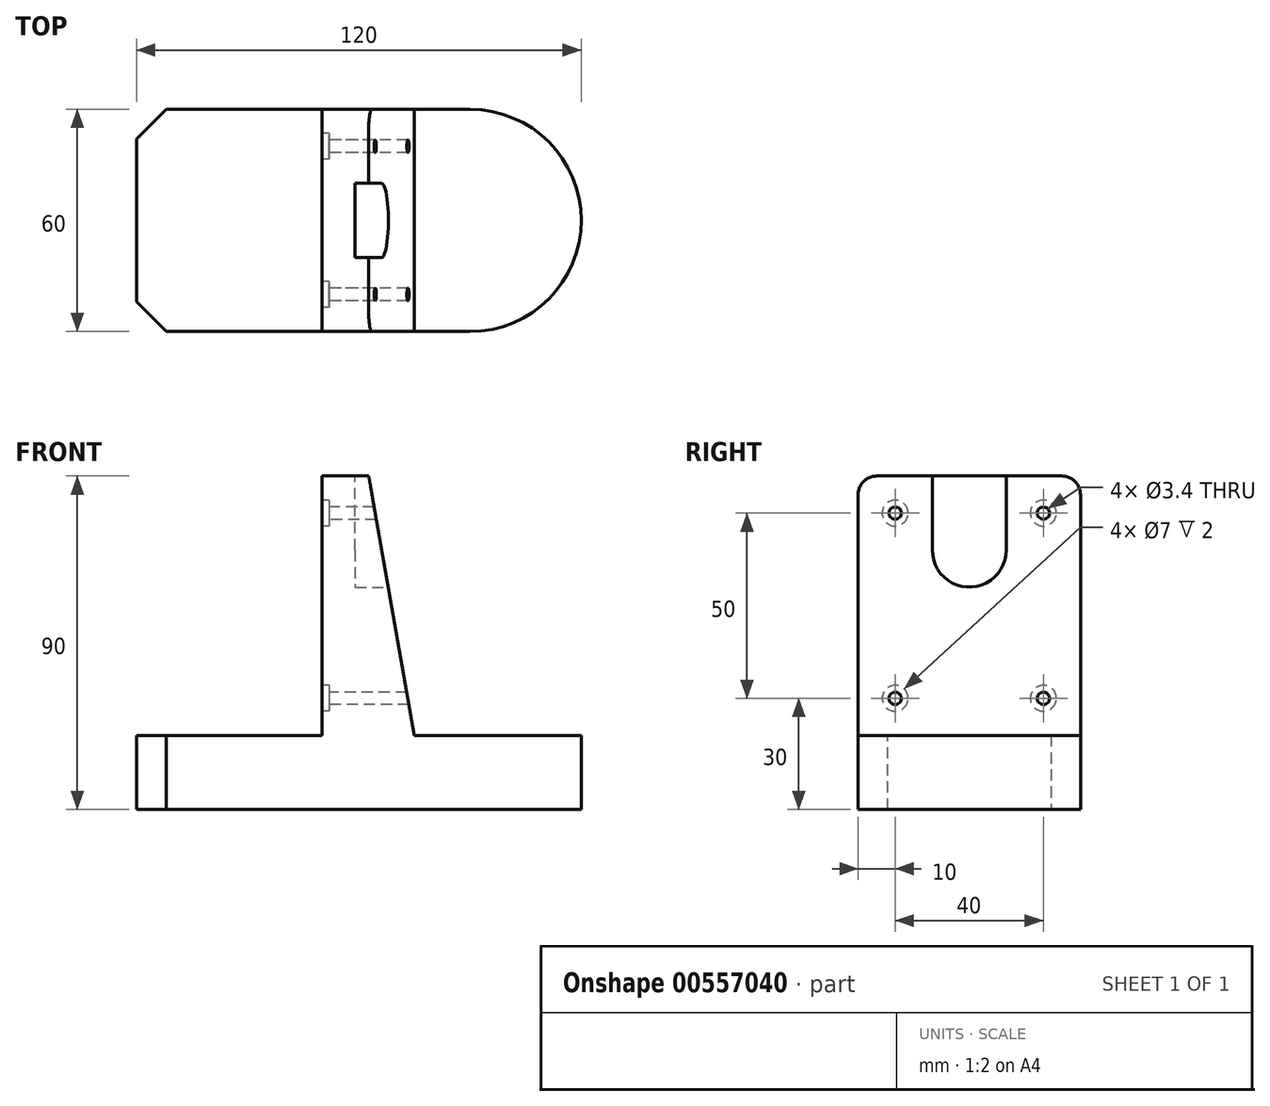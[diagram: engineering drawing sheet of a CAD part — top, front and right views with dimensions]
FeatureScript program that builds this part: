
annotation { "Feature Type Name" : "Feature", "Feature Type Description" : "" }
export const myFeature = defineFeature(function(context is Context, id is Id, definition is map)
    precondition{}
    {
        {
            var Q0;
            Q0=qCreatedBy(makeId("Front.planeOp"),FACE);
            var sketch = newSketch(context, id + "F0", { "sketchPlane" : qUnion([Q0])});
            skLineSegment(sketch, "E0", {"start": v(0, 0) * mm, "end": v(120, 0) * mm});
            skLineSegment(sketch, "E1", {"start": v(0, 0) * mm, "end": v(0, 20) * mm});
            skLineSegment(sketch, "E2", {"start": v(0, 20) * mm, "end": v(50, 20) * mm});
            skLineSegment(sketch, "E3", {"start": v(120, 0) * mm, "end": v(120, 20) * mm});
            skLineSegment(sketch, "E4", {"start": v(75, 20) * mm, "end": v(120, 20) * mm});
            skLineSegment(sketch, "E5", {"start": v(75, 20) * mm, "end": v(75, 90) * mm});
            skLineSegment(sketch, "E6", {"start": v(50, 20) * mm, "end": v(50, 90) * mm});
            skLineSegment(sketch, "E7", {"start": v(50, 90) * mm, "end": v(75, 90) * mm});
            skSolve(sketch);
        }
        {
            var Q0;
            Q0=qSketchRegion(id+"F0",true);
            extrude(context, id + "F1", {"entities" : qUnion([Q0]), "endBound" : BoundingType.SYMMETRIC, "depth" : 60 * mm, "offsetDistance" : 25 * mm});
        }
        {
            var Q0;
            Q0=makeQuery(id+"F1.opExtrude","CAP_EDGE",EDGE,{"disambiguationData":[OSD([sQuery(id+"F0.wireOp",EDGE,"E3")])],"isStart":false});
            var Q1;
            Q1=makeQuery(id+"F1.opExtrude","CAP_EDGE",EDGE,{"disambiguationData":[OSD([sQuery(id+"F0.wireOp",EDGE,"E3")])],"isStart":true});
            fillet(context, id + "F2", {"entities" : qUnion([Q0, Q1]), "radius" : 30 * mm, "tangentPropagation" : true, "allowEdgeOverflow" : false});
        }
        {
            var Q0;
            Q0=makeQuery(id+"F1.opExtrude","SWEPT_FACE",FACE,{"disambiguationData":[OSD([sQuery(id+"F0.wireOp",EDGE,"E6")])]});
            var sketch = newSketch(context, id + "F3", { "sketchPlane" : qUnion([Q0])});
            skLineSegment(sketch, "E8", {"start": v(-20, 30) * mm, "end": v(20, 30) * mm, "construction": true});
            skLineSegment(sketch, "E9", {"start": v(0, 0) * mm, "end": v(0, 92.48) * mm, "construction": true});
            skPoint(sketch, "E9.endSnap0", {"position": v(0, 90) * mm});
            skLineSegment(sketch, "E10", {"start": v(-20, 30) * mm, "end": v(-20, 80) * mm, "construction": true});
            skLineSegment(sketch, "E11", {"start": v(-20, 80) * mm, "end": v(20, 80) * mm, "construction": true});
            skLineSegment(sketch, "E12", {"start": v(20, 80) * mm, "end": v(20, 30) * mm, "construction": true});
            skCircle(sketch, "E13", {"center": v(-20, 80) * mm, "radius": 3.5 * mm});
            skSolve(sketch);
        }
        {
            var Q0;
            Q0=sQuery(id+"F3.wireOp",VERTEX,"E13.center");
            var Q1;
            Q1=sQuery(id+"F3.wireOp",VERTEX,"E8.start");
            var Q2;
            Q2=sQuery(id+"F3.wireOp",VERTEX,"E12.end");
            var Q3;
            Q3=sQuery(id+"F3.wireOp",VERTEX,"E12.start");
            var Q4;
            Q4=makeQuery(id+"F1.opExtrude","SWEPT_BODY",BODY,{"disambiguationData":[OSD([sQuery(id+"F0.wireOp",EDGE,"E0"),sQuery(id+"F0.wireOp",EDGE,"E1"),sQuery(id+"F0.wireOp",EDGE,"E2"),sQuery(id+"F0.wireOp",EDGE,"E3"),sQuery(id+"F0.wireOp",EDGE,"E4"),sQuery(id+"F0.wireOp",EDGE,"E5"),sQuery(id+"F0.wireOp",EDGE,"E6"),sQuery(id+"F0.wireOp",EDGE,"E7")])]});
            hole(context, id + "F4", {"style" : HoleStyle.C_BORE, "endStyle" : HoleEndStyle.THROUGH, "holeDiameter" : 3.4 * mm, "cBoreDiameter" : 7 * mm, "cBoreDepth" : 2 * mm, "isTappedThrough" : true, "tappedDepth" : 12 * mm, "tapClearance" : 3, "locations" : qUnion([Q0, Q1, Q2, Q3]), "scope" : qUnion([Q4])});
        }
        {
            var Q0;
            Q0=makeQuery(id+"F1.opExtrude","CAP_EDGE",EDGE,{"disambiguationData":[OSD([sQuery(id+"F0.wireOp",EDGE,"E1")])],"isStart":true});
            var Q1;
            Q1=makeQuery(id+"F1.opExtrude","CAP_EDGE",EDGE,{"disambiguationData":[OSD([sQuery(id+"F0.wireOp",EDGE,"E1")])],"isStart":false});
            chamfer(context, id + "F5", {"entities" : qUnion([Q0, Q1]), "width" : 8 * mm, "tangentPropagation" : true});
        }
        {
            var Q0;
            Q0=makeQuery(id+"F1.opExtrude","CAP_FACE",FACE,{"disambiguationData":[OSD([sQuery(id+"F0.wireOp",EDGE,"E0"),sQuery(id+"F0.wireOp",EDGE,"E1"),sQuery(id+"F0.wireOp",EDGE,"E2"),sQuery(id+"F0.wireOp",EDGE,"E3"),sQuery(id+"F0.wireOp",EDGE,"E4"),sQuery(id+"F0.wireOp",EDGE,"E5"),sQuery(id+"F0.wireOp",EDGE,"E6"),sQuery(id+"F0.wireOp",EDGE,"E7")])],"isStart":false});
            var sketch = newSketch(context, id + "F6", { "sketchPlane" : qUnion([Q0])});
            skLineSegment(sketch, "E14", {"start": v(75, 20) * mm, "end": v(62.66, 90) * mm});
            skSolve(sketch);
        }
        {
            var Q0;
            Q0=makeQuery(id+"F1.opExtrude","SWEPT_FACE",FACE,{"disambiguationData":[OSD([sQuery(id+"F0.wireOp",EDGE,"E5")])]});
            var sketch = newSketch(context, id + "F7", { "sketchPlane" : qUnion([Q0])});
            skLineSegment(sketch, "E15", {"start": v(0, -24) * mm, "end": v(0, 77.1) * mm, "construction": true});
            skLineSegment(sketch, "E16", {"start": v(-10, 70) * mm, "end": v(10, 70) * mm, "construction": true});
            skCircle(sketch, "E17", {"center": v(0, 70) * mm, "radius": 10 * mm});
            skLineSegment(sketch, "E18", {"start": v(-10, 70) * mm, "end": v(-10, 90) * mm});
            skLineSegment(sketch, "E19", {"start": v(10, 70) * mm, "end": v(10, 90) * mm});
            skSolve(sketch);
        }
        {
            var Q0;
            Q0=makeQuery(id+"F1.opExtrude","CAP_FACE",FACE,{"disambiguationData":[OSD([sQuery(id+"F0.wireOp",EDGE,"E0"),sQuery(id+"F0.wireOp",EDGE,"E1"),sQuery(id+"F0.wireOp",EDGE,"E2"),sQuery(id+"F0.wireOp",EDGE,"E3"),sQuery(id+"F0.wireOp",EDGE,"E4"),sQuery(id+"F0.wireOp",EDGE,"E5"),sQuery(id+"F0.wireOp",EDGE,"E6"),sQuery(id+"F0.wireOp",EDGE,"E7")])],"isStart":false});
            var sketch = newSketch(context, id + "F8", { "sketchPlane" : qUnion([Q0])});
            skLineSegment(sketch, "E20", {"start": v(75, 60) * mm, "end": v(59, 60) * mm});
            skLineSegment(sketch, "E21", {"start": v(59, 60) * mm, "end": v(59, 90) * mm});
            skSolve(sketch);
        }
        {
            var Q0;
            Q0=makeQuery(id+"F1.opExtrude","SWEPT_FACE",FACE,{"disambiguationData":[OSD([sQuery(id+"F0.wireOp",EDGE,"E6")])]});
            var Q1;
            Q1=sQuery(id+"F8.wireOp",VERTEX,"E21.start");
            cPlane(context, id + "F9", {"entities" : qUnion([Q0, Q1]), "cplaneType" : CPlaneType.PLANE_POINT, "offset" : 25 * mm, "width" : 150 * mm, "height" : 150 * mm});
        }
        {
            var Q0;
            {var subQ0=sQuery(id+"F7.wireOp",EDGE,"E18");Q0=makeQuery(id+"F7.imprint","IMPRINT",FACE,{"disambiguationData":[TD([[makeQuery(id+"F7.imprint","IMPRINT",EDGE,{"derivedFrom":subQ0}),-1.0]])]});}
            var Q1;
            {var subQ0=sQuery(id+"F7.wireOp",EDGE,"E17");var subQ1=makeQuery(id+"F7.imprint","INTERSECT",VERTEX,{"derivedFrom":[subQ0,sQuery(id+"F7.wireOp",EDGE,"E18")]});Q1=makeQuery(id+"F7.imprint","IMPRINT",FACE,{"disambiguationData":[TD([[makeQuery(id+"F7.imprint","IMPRINT",EDGE,{"disambiguationData":[TD([[subQ1,1.0]])],"derivedFrom":subQ0}),1.0]])]});}
            var Q2;
            Q2=qCreatedBy(id+"F9.planeOp",FACE);
            extrude(context, id + "F10", {"entities" : qUnion([Q0, Q1]), "operationType" : NewBodyOperationType.REMOVE, "endBound" : BoundingType.UP_TO_SURFACE, "oppositeDirection" : true, "depth" : 25 * mm, "endBoundEntityFace" : qUnion([Q2]), "offsetDistance" : 25 * mm});
        }
        {
            var Q0;
            {var subQ0=sQuery(id+"F6.wireOp",EDGE,"E14");Q0=makeQuery(id+"F6.imprint","IMPRINT",FACE,{"disambiguationData":[TD([[makeQuery(id+"F6.imprint","IMPRINT",EDGE,{"derivedFrom":subQ0}),-1.0]])]});}
            extrude(context, id + "F11", {"entities" : qUnion([Q0]), "operationType" : NewBodyOperationType.REMOVE, "endBound" : BoundingType.THROUGH_ALL, "oppositeDirection" : true, "depth" : 25 * mm, "offsetDistance" : 25 * mm});
        }
        {
            var Q0;
            Q0=makeQuery(id+"F1.opExtrude","CAP_EDGE",EDGE,{"disambiguationData":[OSD([sQuery(id+"F0.wireOp",EDGE,"E7")])],"isStart":false});
            var Q1;
            Q1=makeQuery(id+"F1.opExtrude","CAP_EDGE",EDGE,{"disambiguationData":[OSD([sQuery(id+"F0.wireOp",EDGE,"E7")])],"isStart":true});
            fillet(context, id + "F12", {"entities" : qUnion([Q0, Q1]), "radius" : 5 * mm, "tangentPropagation" : true, "allowEdgeOverflow" : false});
        }
    });
